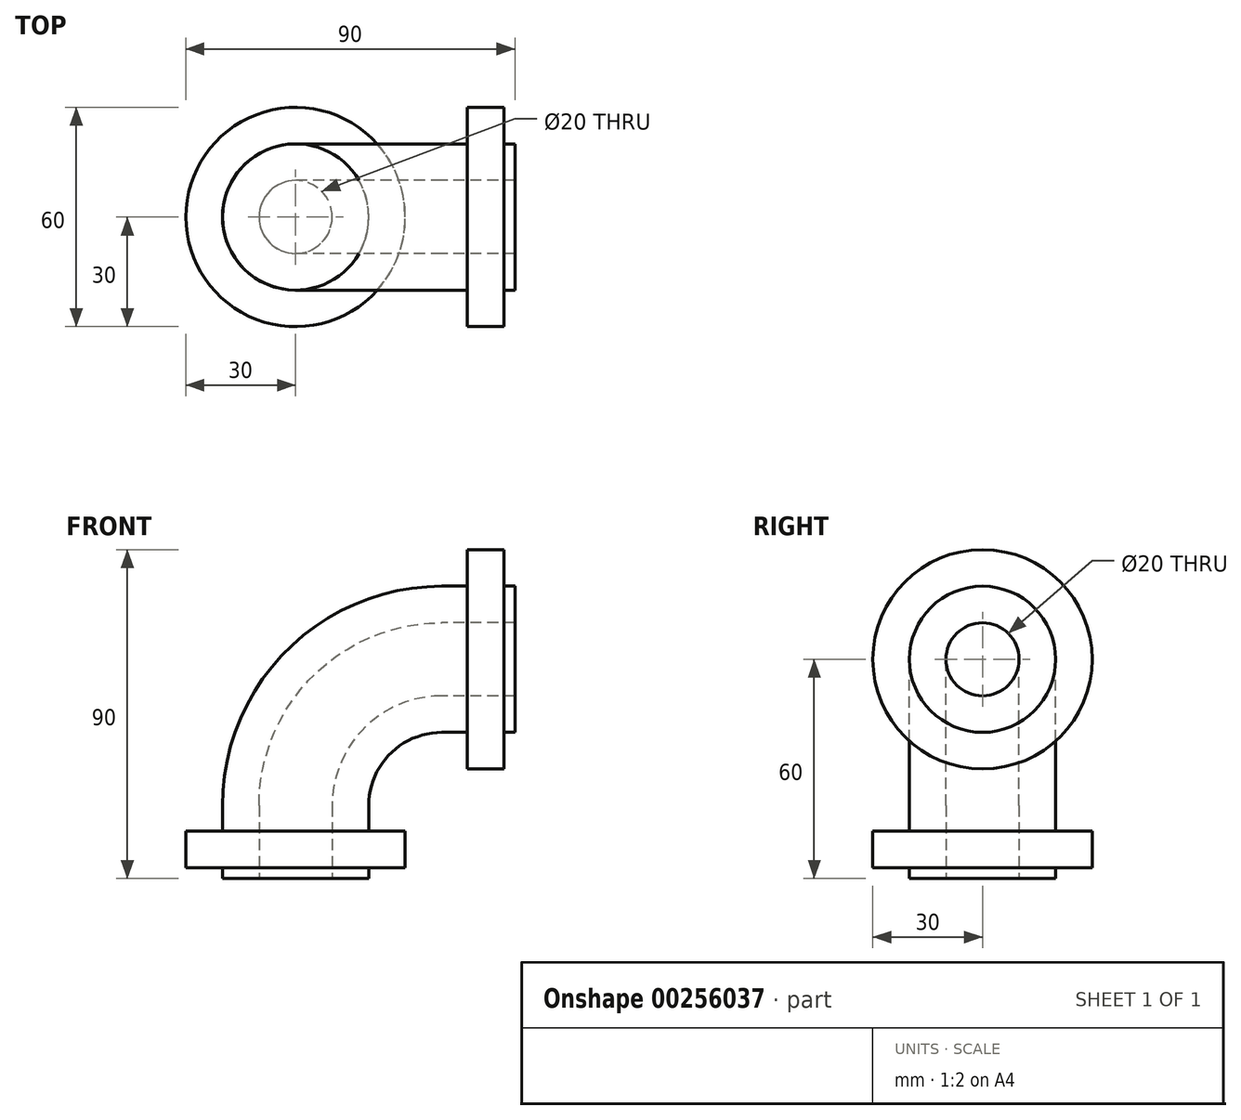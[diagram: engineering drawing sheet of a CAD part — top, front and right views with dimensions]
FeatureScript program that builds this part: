
annotation { "Feature Type Name" : "Feature", "Feature Type Description" : "" }
export const myFeature = defineFeature(function(context is Context, id is Id, definition is map)
    precondition{}
    {
        {
            var Q0;
            Q0=qCreatedBy(makeId("Right.planeOp"),FACE);
            var sketch = newSketch(context, id + "F0", { "sketchPlane" : qUnion([Q0])});
            skCircle(sketch, "E0", {"center": v(0, 0) * mm, "radius": 10 * mm});
            skCircle(sketch, "E1", {"center": v(0, 0) * mm, "radius": 20 * mm});
            skSolve(sketch);
        }
        {
            var Q0;
            Q0=qCreatedBy(makeId("Front.planeOp"),FACE);
            var sketch = newSketch(context, id + "F1", { "sketchPlane" : qUnion([Q0])});
            skLineSegment(sketch, "E2", {"start": v(0, 0) * mm, "end": v(-20, 0) * mm});
            skArc(sketch, "E3", {"start": v(-20, 0) * mm, "mid": v(-48.28, -11.72) * mm, "end": v(-60, -40) * mm});
            skLineSegment(sketch, "E4", {"start": v(-60, -40) * mm, "end": v(-60, -60) * mm});
            skSolve(sketch);
        }
        {
            var Q0;
            Q0=makeQuery(id+"F0.imprint","IMPRINT",FACE,{"disambiguationData":[TD([[makeQuery(id+"F0.imprint","IMPRINT",EDGE,{"derivedFrom":sQuery(id+"F0.wireOp",EDGE,"E0")}),-1.0]])]});
            var Q1;
            Q1=sQuery(id+"F1.wireOp",EDGE,"E2");
            var Q2;
            Q2=sQuery(id+"F1.wireOp",EDGE,"E3");
            var Q3;
            Q3=sQuery(id+"F1.wireOp",EDGE,"E4");
            sweep(context, id + "F2", {"profiles" : qUnion([Q0]), "path" : qUnion([Q1, Q2, Q3])});
        }
        {
            var Q0;
            Q0=qCreatedBy(makeId("Right.planeOp"),FACE);
            cPlane(context, id + "F3", {"entities" : qUnion([Q0]), "cplaneType" : CPlaneType.OFFSET, "offset" : 3 * mm, "oppositeDirection" : true, "width" : 150 * mm, "height" : 150 * mm});
        }
        {
            var Q0;
            Q0=qCreatedBy(id+"F3.planeOp",FACE);
            var sketch = newSketch(context, id + "F4", { "sketchPlane" : qUnion([Q0])});
            skCircle(sketch, "E5.0", {"center": v(0, 0) * mm, "radius": 20 * mm});
            skCircle(sketch, "E6", {"center": v(0, 0) * mm, "radius": 30 * mm});
            skSolve(sketch);
        }
        {
            var Q0;
            Q0=makeQuery(id+"F4.imprint","IMPRINT",FACE,{"disambiguationData":[TD([[makeQuery(id+"F4.imprint","IMPRINT",EDGE,{"derivedFrom":sQuery(id+"F4.wireOp",EDGE,"E5.0")}),-1.0]])]});
            extrude(context, id + "F5", {"entities" : qUnion([Q0]), "operationType" : NewBodyOperationType.ADD, "oppositeDirection" : true, "depth" : 10 * mm});
        }
        {
            var Q0;
            Q0=makeQuery(id+"F2.opSweep","CAP_FACE",FACE,{"disambiguationData":[OSD([sQuery(id+"F0.wireOp",EDGE,"E0"),sQuery(id+"F0.wireOp",EDGE,"E1"),sQuery(id+"F1.wireOp",VERTEX,"E4.end")])],"isStart":false});
            cPlane(context, id + "F6", {"entities" : qUnion([Q0]), "cplaneType" : CPlaneType.OFFSET, "offset" : 3 * mm, "oppositeDirection" : true, "width" : 150 * mm, "height" : 150 * mm});
        }
        {
            var Q0;
            Q0=qCreatedBy(id+"F6.planeOp",FACE);
            var sketch = newSketch(context, id + "F7", { "sketchPlane" : qUnion([Q0])});
            skCircle(sketch, "E7.0", {"center": v(-60, 0) * mm, "radius": 20 * mm});
            skCircle(sketch, "E8", {"center": v(-60, 0) * mm, "radius": 30 * mm});
            skSolve(sketch);
        }
        {
            var Q0;
            Q0=makeQuery(id+"F7.imprint","IMPRINT",FACE,{"disambiguationData":[TD([[makeQuery(id+"F7.imprint","IMPRINT",EDGE,{"derivedFrom":sQuery(id+"F7.wireOp",EDGE,"E7.0")}),-1.0]])]});
            extrude(context, id + "F8", {"entities" : qUnion([Q0]), "operationType" : NewBodyOperationType.ADD, "oppositeDirection" : true, "depth" : 10 * mm});
        }
    });
